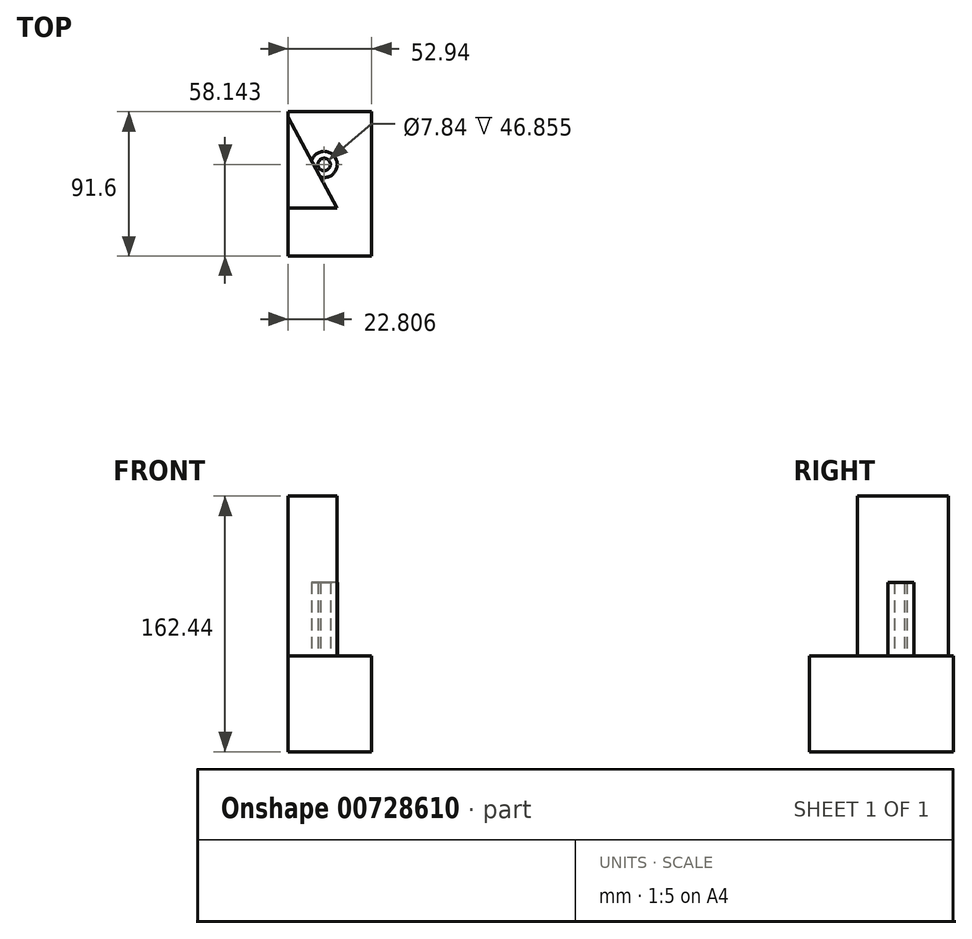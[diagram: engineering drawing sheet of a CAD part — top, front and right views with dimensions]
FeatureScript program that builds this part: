
annotation { "Feature Type Name" : "Feature", "Feature Type Description" : "" }
export const myFeature = defineFeature(function(context is Context, id is Id, definition is map)
    precondition{}
    {
        {
            var Q0;
            Q0=qCreatedBy(makeId("Right.planeOp"),FACE);
            var sketch = newSketch(context, id + "F0", { "sketchPlane" : qUnion([Q0])});
            skLineSegment(sketch, "E0.bottom", {"start": v(61, 54.8) * mm, "end": v(-30.6, 54.8) * mm});
            skLineSegment(sketch, "E0.top", {"start": v(61, -5.96) * mm, "end": v(-30.6, -5.96) * mm});
            skLineSegment(sketch, "E0.left", {"start": v(61, 54.8) * mm, "end": v(61, -5.96) * mm});
            skLineSegment(sketch, "E0.right", {"start": v(-30.6, 54.8) * mm, "end": v(-30.6, -5.96) * mm});
            skPoint(sketch, "E0.middle", {"position": v(15.2, 24.43) * mm});
            skSolve(sketch);
        }
        {
            var Q0;
            Q0 = qSketchRegion(id + "F0", true);
            extrude(context, id + "F1", {"entities" : qUnion([Q0]), "depth" : 52.94 * mm, "offsetDistance" : 25.4 * mm});
        }
        {
            var Q0;
            Q0=makeQuery(id+"F1.opExtrude","SWEPT_FACE",FACE,{"disambiguationData":[OSD([sQuery(id+"F0.wireOp",EDGE,"E0.bottom")])]});
            var sketch = newSketch(context, id + "F2", { "sketchPlane" : qUnion([Q0])});
            skCircle(sketch, "E1", {"center": v(22.8, 27.55) * mm, "radius": 8.33 * mm});
            skCircle(sketch, "E2", {"center": v(22.8, 27.55) * mm, "radius": 3.92 * mm});
            skSolve(sketch);
        }
        {
            var Q0;
            Q0 = qSketchRegion(id + "F2", true);
            extrude(context, id + "F3", {"entities" : qUnion([Q0]), "operationType" : NewBodyOperationType.ADD, "depth" : 46.85 * mm, "offsetDistance" : 25.4 * mm});
        }
        {
            var Q0;
            {var subQ1=sQuery(id+"F0.wireOp",EDGE,"E0.left");var subQ3=sQuery(id+"F0.wireOp",EDGE,"E0.bottom");Q0=makeQuery(id+"F3.boolean.opBoolean","SPLIT",FACE,{"disambiguationData":[TD([makeQuery(id+"F1.opExtrude","SWEPT_FACE",FACE,{"disambiguationData":[OSD([subQ1])]})])],"derivedFrom":makeQuery(id+"F1.opExtrude","SWEPT_FACE",FACE,{"disambiguationData":[OSD([subQ3])]})});}
            var sketch = newSketch(context, id + "F4", { "sketchPlane" : qUnion([Q0])});
            skSolve(sketch);
        }
        {
            var Q0;
            {var subQ0=sQuery(id+"F0.wireOp",EDGE,"E0.bottom");Q0=makeQuery(id+"F4.imprint","IMPRINT",FACE,{"disambiguationData":[TD([[makeQuery(id+"F4.imprint","IMPRINT",EDGE,{"derivedFrom":makeQuery(id+"F1.opExtrude","CAP_EDGE",EDGE,{"disambiguationData":[OSD([subQ0])],"isStart":true})}),1.0]])]});}
            var sketch = newSketch(context, id + "F5", { "sketchPlane" : qUnion([Q0])});
            skLineSegment(sketch, "E3", {"start": v(30.91, 0) * mm, "end": v(0, 57.65) * mm});
            skLineSegment(sketch, "E4", {"start": v(0, 57.65) * mm, "end": v(0, 0) * mm});
            skLineSegment(sketch, "E5", {"start": v(0, 0) * mm, "end": v(30.91, 0) * mm});
            skLineSegment(sketch, "E6", {"start": v(20.87, 18.73) * mm, "end": v(20.87, 18.73) * mm});
            skSolve(sketch);
        }
        {
            var Q0;
            Q0 = qSketchRegion(id + "F5", true);
            extrude(context, id + "F6", {"entities" : qUnion([Q0]), "operationType" : NewBodyOperationType.ADD, "depth" : 101.67 * mm, "offsetDistance" : 25.4 * mm});
        }
    });
